# Revit family: Блок-переключатель для 3-х трубных систем EHCH-160D
name_source: partatom
category: Mechanical Equipment
revit_build: Autodesk Revit 2016 (Build: 20150506_1715(x64)
units: mm (PartAtom-declared; Revit-internal decimal feet)

## family parameters
Cut with Voids When Loaded = No
Host = Face
Part Type = Normal
Room Calculation Point = No
Round Connector Dimension = Use Diameter
Shared = No

## types (1)
- EHCH-160D
    Default Elevation = 1219.2 mm  [stored 4 ft]
    Артикул = 1040585
    Вес = 7.00 kg
    Высота = 191 mm  [stored 0.62664 ft]
    Глубина = 214 mm  [stored 0.7021 ft]
    Максимальная потребляемая мощность = 0.02 kW
    Максимальное кол-во подключаемых внутренних блоков, шт = 7
    Максимальный ток = 0 A
    Модель = EHCH-160D
    Наименование = Блок-переключатель для 3-х трубных систем
    Производитель = Electrolux
    Таблица модель = Модель
    Таблица наименование = Наименование
    Таблица параметров = Таблица параметров
    Таблица частота сети = Частота сети
    Таблица электропитание = Электропитание
    Фаза = 1
    Частота сети = 50 Hz
    Ширина = 301 mm  [stored 0.987533 ft]
    Эл. питание(коннектор) = 220 V
    Электропитание, (В) = 220

note: [stored X ft] marks values corroborated as IEEE doubles in the binary element streams (Revit-internal decimal feet)
